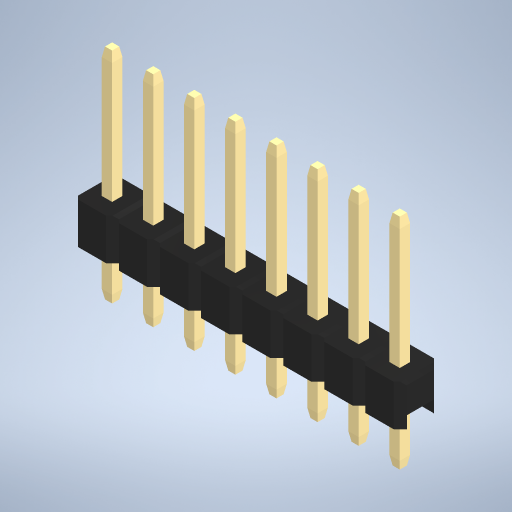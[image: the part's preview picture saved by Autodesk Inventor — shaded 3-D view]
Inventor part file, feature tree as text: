
AUTODESK INVENTOR PART (.ipt)
format: ipt  version: 2023.1 (Build 271208000, 208)  size: 423,936 bytes
history: native  units: in
note: dims shown in document units (in); Inventor stores cm internally (conversion verified against a paired STEP export)
features: other x7, chamfer x1, boolean_combine x1
ambient origin geometry x8: Origin, YZ Plane, XZ Plane, XY Plane, X Axis, Y Axis, Z Axis, Center Point
bodies: Solid1 (feature_tree), Solid2 (feature_tree), Solid3 (feature_tree), Solid4 (feature_tree), Solid5 (feature_tree), Solid6 (feature_tree), Solid7 (feature_tree), Solid8 (feature_tree), Solid9 (feature_tree)
feature tree (9):
  chamfer  "Chamfer3"  [1 undecoded]
  other  "LPattern1[1]"
  other  "LPattern1[2]"
  other  "LPattern1[3]"
  other  "LPattern1[4]"
  other  "LPattern1[5]"
  other  "LPattern1[6]"
  other  "LPattern1[7]"
  boolean_combine  "Combine1"
note: 1 required parameter value undecoded (feature->parameter linkage not recoverable at this tier; creation-order binding heuristic only, values carry confidence <= 0.55)
